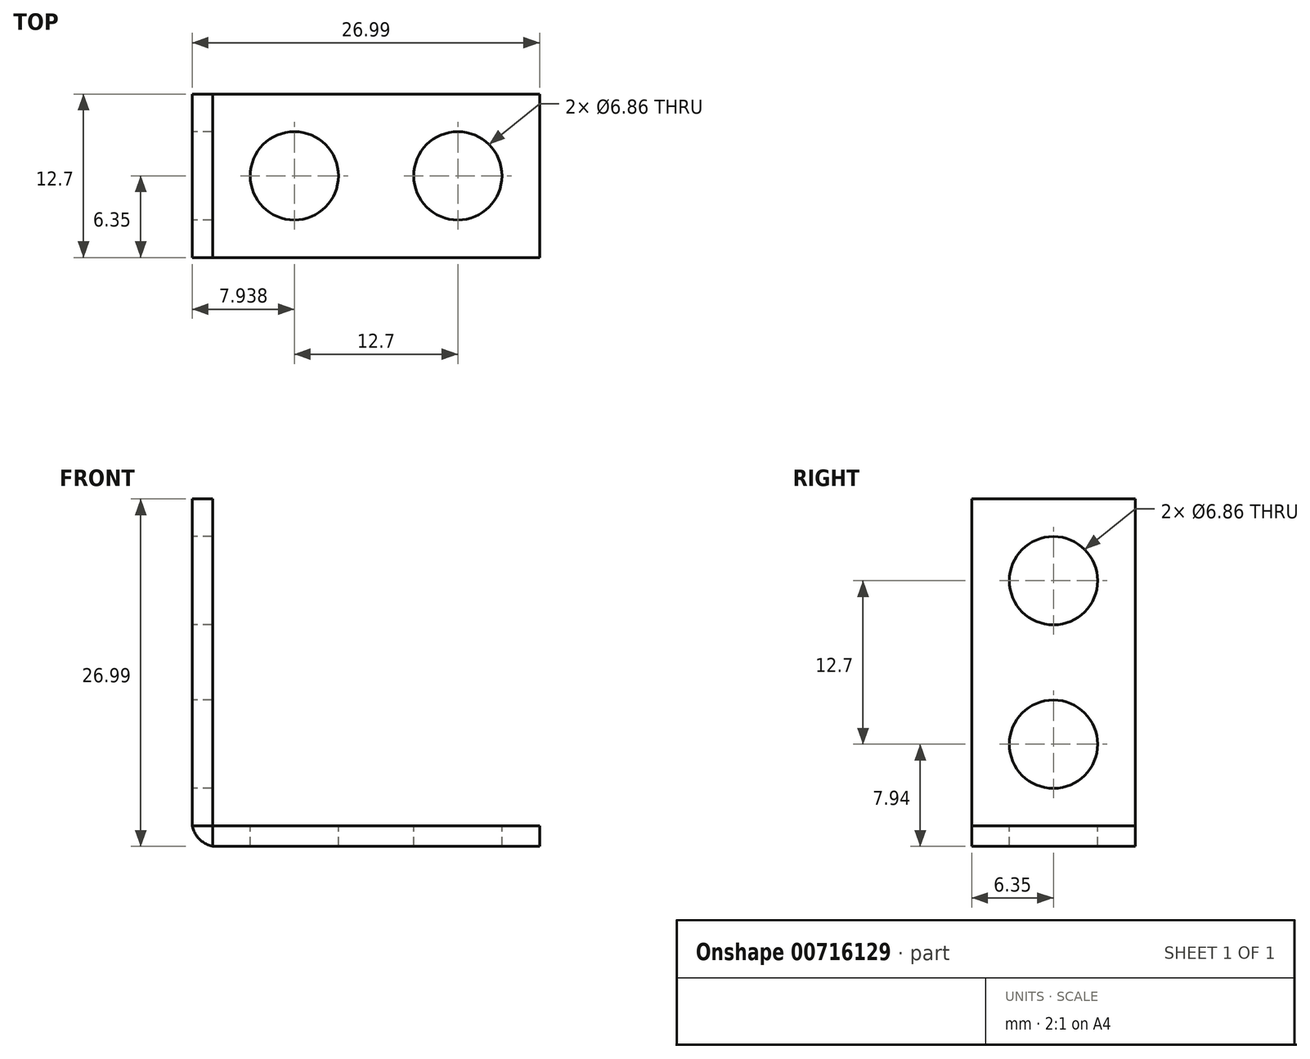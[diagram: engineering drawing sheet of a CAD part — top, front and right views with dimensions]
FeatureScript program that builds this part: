
annotation { "Feature Type Name" : "Feature", "Feature Type Description" : "" }
export const myFeature = defineFeature(function(context is Context, id is Id, definition is map)
    precondition{}
    {
        {
            var Q0;
            Q0=qCreatedBy(makeId("Right.planeOp"),FACE);
            var sketch = newSketch(context, id + "F0", { "sketchPlane" : qUnion([Q0])});
            skLineSegment(sketch, "E0.bottom", {"start": v(0, 0) * mm, "end": v(12.7, 0) * mm});
            skLineSegment(sketch, "E0.top", {"start": v(0, 25.4) * mm, "end": v(12.7, 25.4) * mm});
            skLineSegment(sketch, "E0.left", {"start": v(0, 0) * mm, "end": v(0, 25.4) * mm});
            skLineSegment(sketch, "E0.right", {"start": v(12.7, 0) * mm, "end": v(12.7, 25.4) * mm});
            skLineSegment(sketch, "E1", {"start": v(6.35, 25.4) * mm, "end": v(6.35, 19.05) * mm});
            skCircle(sketch, "E2", {"center": v(6.35, 19.05) * mm, "radius": 3.43 * mm});
            skLineSegment(sketch, "E3", {"start": v(6.35, 6.35) * mm, "end": v(6.35, 0) * mm});
            skCircle(sketch, "E4", {"center": v(6.35, 6.35) * mm, "radius": 3.43 * mm});
            skLineSegment(sketch, "E5", {"start": v(6.35, 19.05) * mm, "end": v(6.35, 12.7) * mm});
            skLineSegment(sketch, "E6", {"start": v(6.35, 12.7) * mm, "end": v(6.35, 6.35) * mm});
            skSolve(sketch);
        }
        {
            var Q0;
            Q0 = qSketchRegion(id + "F0", true);
            extrude(context, id + "F1", {"entities" : qUnion([Q0]), "depth" : 1.59 * mm, "offsetDistance" : 25.4 * mm});
        }
        {
            var Q0;
            Q0=qCreatedBy(makeId("Top.planeOp"),FACE);
            var sketch = newSketch(context, id + "F2", { "sketchPlane" : qUnion([Q0])});
            skLineSegment(sketch, "E7.bottom", {"start": v(1.59, 0) * mm, "end": v(26.99, 0) * mm});
            skLineSegment(sketch, "E7.top", {"start": v(1.59, 12.7) * mm, "end": v(26.99, 12.7) * mm});
            skLineSegment(sketch, "E7.left", {"start": v(1.59, 0) * mm, "end": v(1.59, 12.7) * mm});
            skLineSegment(sketch, "E7.right", {"start": v(26.99, 0) * mm, "end": v(26.99, 12.7) * mm});
            skLineSegment(sketch, "E8", {"start": v(20.64, 6.35) * mm, "end": v(26.99, 6.35) * mm});
            skCircle(sketch, "E9", {"center": v(20.64, 6.35) * mm, "radius": 3.43 * mm});
            skLineSegment(sketch, "E10", {"start": v(1.59, 6.35) * mm, "end": v(7.94, 6.35) * mm});
            skLineSegment(sketch, "E11", {"start": v(7.94, 6.35) * mm, "end": v(14.29, 6.35) * mm});
            skLineSegment(sketch, "E12", {"start": v(14.29, 6.35) * mm, "end": v(20.64, 6.35) * mm});
            skCircle(sketch, "E13", {"center": v(7.94, 6.35) * mm, "radius": 3.43 * mm});
            skSolve(sketch);
        }
        {
            var Q0;
            Q0 = qSketchRegion(id + "F2", true);
            extrude(context, id + "F3", {"entities" : qUnion([Q0]), "operationType" : NewBodyOperationType.ADD, "oppositeDirection" : true, "depth" : 1.59 * mm, "offsetDistance" : 25.4 * mm});
        }
        {
            var Q0;
            Q0=qCreatedBy(makeId("Front.planeOp"),FACE);
            var sketch = newSketch(context, id + "F4", { "sketchPlane" : qUnion([Q0])});
            skLineSegment(sketch, "E14.bottom", {"start": v(1.59, 0) * mm, "end": v(0, 0) * mm});
            skLineSegment(sketch, "E14.top", {"start": v(1.59, -1.59) * mm, "end": v(0, -1.59) * mm});
            skLineSegment(sketch, "E14.left", {"start": v(1.59, 0) * mm, "end": v(1.59, -1.59) * mm});
            skLineSegment(sketch, "E14.right", {"start": v(0, 0) * mm, "end": v(0, -1.59) * mm});
            skSolve(sketch);
        }
        {
            var Q0;
            Q0 = qSketchRegion(id + "F4", true);
            var Q1;
            Q1=makeQuery(id+"F3.opExtrude","SWEPT_FACE",FACE,{"disambiguationData":[OSD([sQuery(id+"F2.wireOp",EDGE,"E7.top")])]});
            extrude(context, id + "F5", {"entities" : qUnion([Q0]), "endBound" : BoundingType.UP_TO_SURFACE, "oppositeDirection" : true, "depth" : 25.4 * mm, "endBoundEntityFace" : qUnion([Q1]), "offsetDistance" : 25.4 * mm});
        }
        {
            var Q0;
            Q0=makeQuery(id+"F5.opExtrude","SWEPT_EDGE",EDGE,{"disambiguationData":[OSD([sQuery(id+"F4.wireOp",EDGE,"E14.top"),sQuery(id+"F4.wireOp",EDGE,"E14.right")])]});
            fillet(context, id + "F6", {"entities" : qUnion([Q0]), "radius" : 2.26 * mm, "tangentPropagation" : true, "rho" : 0.5, "crossSection" : FilletCrossSection.CONIC, "allowEdgeOverflow" : false});
        }
    });
